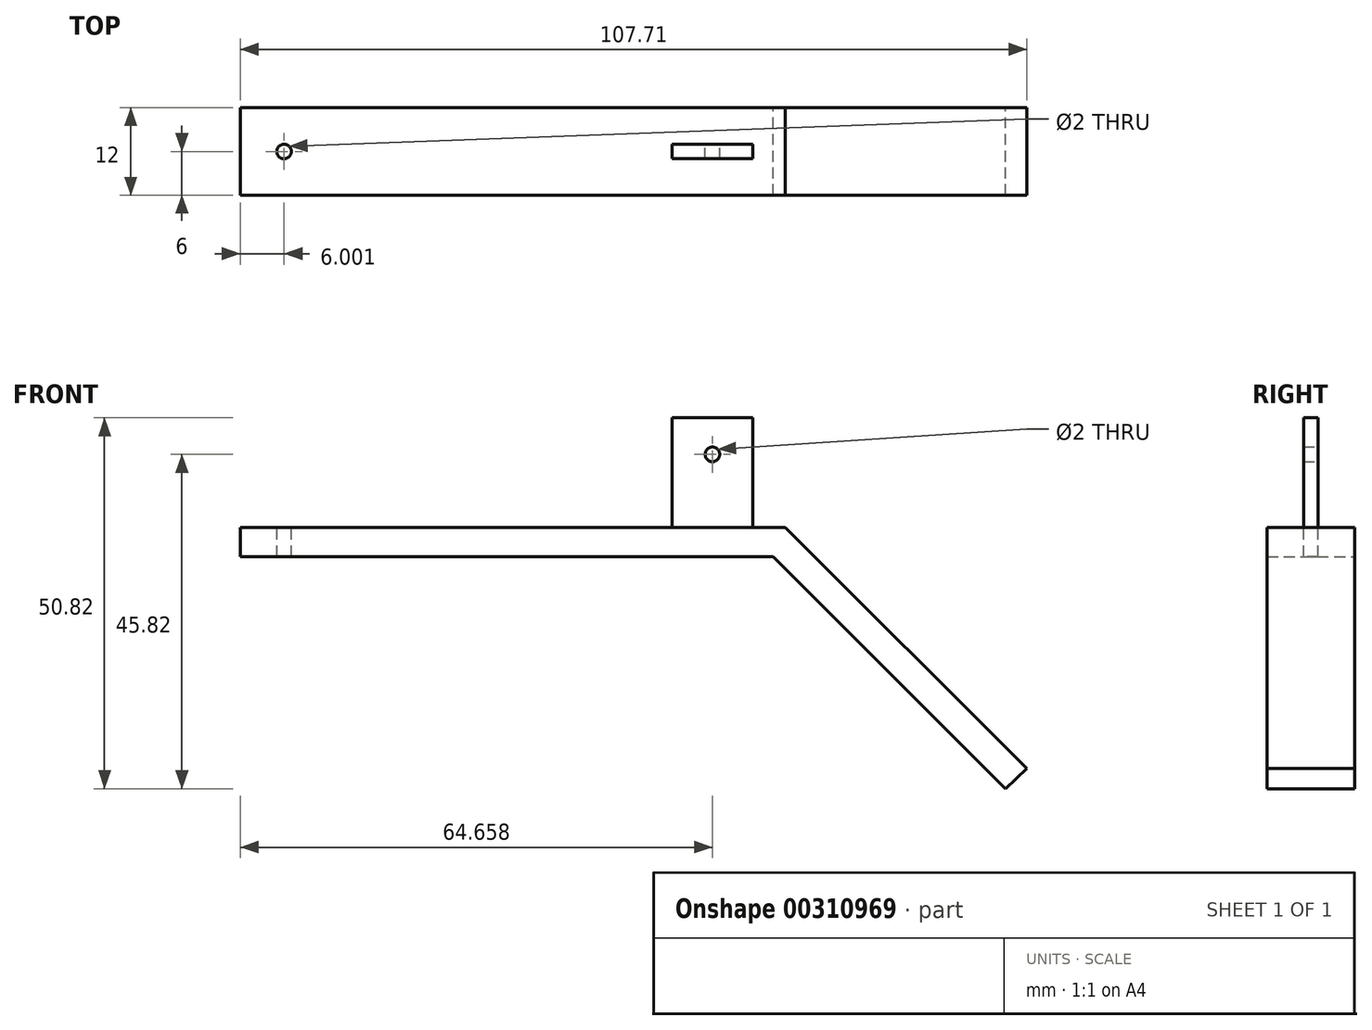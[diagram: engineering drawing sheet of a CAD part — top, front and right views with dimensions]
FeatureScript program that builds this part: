
annotation { "Feature Type Name" : "Feature", "Feature Type Description" : "" }
export const myFeature = defineFeature(function(context is Context, id is Id, definition is map)
    precondition{}
    {
        {
            var Q0;
            Q0=qCreatedBy(makeId("Front.planeOp"),FACE);
            var sketch = newSketch(context, id + "F0", { "sketchPlane" : qUnion([Q0])});
            skLineSegment(sketch, "E0", {"start": v(-64.94, 0) * mm, "end": v(8.06, 0) * mm});
            skLineSegment(sketch, "E1", {"start": v(8.06, 0) * mm, "end": v(39.88, -31.82) * mm});
            skLineSegment(sketch, "E2", {"start": v(-64.94, 0) * mm, "end": v(-64.94, 4) * mm});
            skLineSegment(sketch, "E3", {"start": v(-64.94, 4) * mm, "end": v(9.72, 4) * mm});
            skLineSegment(sketch, "E4", {"start": v(9.72, 4) * mm, "end": v(42.77, -29.05) * mm});
            skLineSegment(sketch, "E5", {"start": v(39.88, -31.82) * mm, "end": v(42.77, -29.05) * mm});
            skSolve(sketch);
        }
        {
            var Q0;
            Q0=makeQuery(id+"F0.imprint","IMPRINT",FACE,{"disambiguationData":[TD([[makeQuery(id+"F0.imprint","IMPRINT",EDGE,{"derivedFrom":sQuery(id+"F0.wireOp",EDGE,"E0")}),1.0]])]});
            extrude(context, id + "F1", {"entities" : qUnion([Q0]), "depth" : 12 * mm});
        }
        {
            var Q0;
            Q0=makeQuery(id+"F1.opExtrude","SWEPT_FACE",FACE,{"disambiguationData":[OSD([sQuery(id+"F0.wireOp",EDGE,"E3")])]});
            var sketch = newSketch(context, id + "F2", { "sketchPlane" : qUnion([Q0])});
            skLineSegment(sketch, "E6.bottom", {"start": v(-5.78, -7) * mm, "end": v(5.22, -7) * mm});
            skLineSegment(sketch, "E6.top", {"start": v(-5.78, -5) * mm, "end": v(5.22, -5) * mm});
            skLineSegment(sketch, "E6.left", {"start": v(-5.78, -7) * mm, "end": v(-5.78, -5) * mm});
            skLineSegment(sketch, "E6.right", {"start": v(5.22, -7) * mm, "end": v(5.22, -5) * mm});
            skPoint(sketch, "E6.middle", {"position": v(-0.28, -6) * mm});
            skPoint(sketch, "E6.middle.positionSnap0", {"position": v(9.72, -6) * mm});
            skPoint(sketch, "E6.centerSnap0", {"position": v(9.72, -6) * mm});
            skSolve(sketch);
        }
        {
            var Q0;
            Q0=makeQuery(id+"F2.imprint","IMPRINT",FACE,{"disambiguationData":[TD([[makeQuery(id+"F2.imprint","IMPRINT",EDGE,{"derivedFrom":sQuery(id+"F2.wireOp",EDGE,"E6.bottom")}),1.0]])]});
            extrude(context, id + "F3", {"entities" : qUnion([Q0]), "operationType" : NewBodyOperationType.ADD, "depth" : 15 * mm});
        }
        {
            var Q0;
            Q0=makeQuery(id+"F3.opExtrude","SWEPT_FACE",FACE,{"disambiguationData":[OSD([sQuery(id+"F2.wireOp",EDGE,"E6.top")])]});
            var sketch = newSketch(context, id + "F4", { "sketchPlane" : qUnion([Q0])});
            skCircle(sketch, "E7", {"center": v(0.28, 14) * mm, "radius": 1 * mm});
            skPoint(sketch, "E7.centerSnap0", {"position": v(0.28, 19) * mm});
            skSolve(sketch);
        }
        {
            var Q0;
            Q0=makeQuery(id+"F4.imprint","IMPRINT",FACE,{"disambiguationData":[TD([[makeQuery(id+"F4.imprint","IMPRINT",EDGE,{"derivedFrom":sQuery(id+"F4.wireOp",EDGE,"E7")}),1.0]])]});
            extrude(context, id + "F5", {"entities" : qUnion([Q0]), "operationType" : NewBodyOperationType.REMOVE, "endBound" : BoundingType.THROUGH_ALL, "oppositeDirection" : true, "depth" : 25 * mm});
        }
        {
            var Q0;
            Q0=makeQuery(id+"F1.opExtrude","SWEPT_FACE",FACE,{"disambiguationData":[OSD([sQuery(id+"F0.wireOp",EDGE,"E3")])]});
            var sketch = newSketch(context, id + "F6", { "sketchPlane" : qUnion([Q0])});
            skCircle(sketch, "E8", {"center": v(-58.94, -6) * mm, "radius": 1 * mm});
            skPoint(sketch, "E8.centerSnap0", {"position": v(-64.94, -6) * mm});
            skSolve(sketch);
        }
        {
            var Q0;
            Q0=makeQuery(id+"F6.imprint","IMPRINT",FACE,{"disambiguationData":[TD([[makeQuery(id+"F6.imprint","IMPRINT",EDGE,{"derivedFrom":sQuery(id+"F6.wireOp",EDGE,"E8")}),1.0]])]});
            extrude(context, id + "F7", {"entities" : qUnion([Q0]), "operationType" : NewBodyOperationType.REMOVE, "endBound" : BoundingType.THROUGH_ALL, "oppositeDirection" : true, "depth" : 25 * mm});
        }
    });
